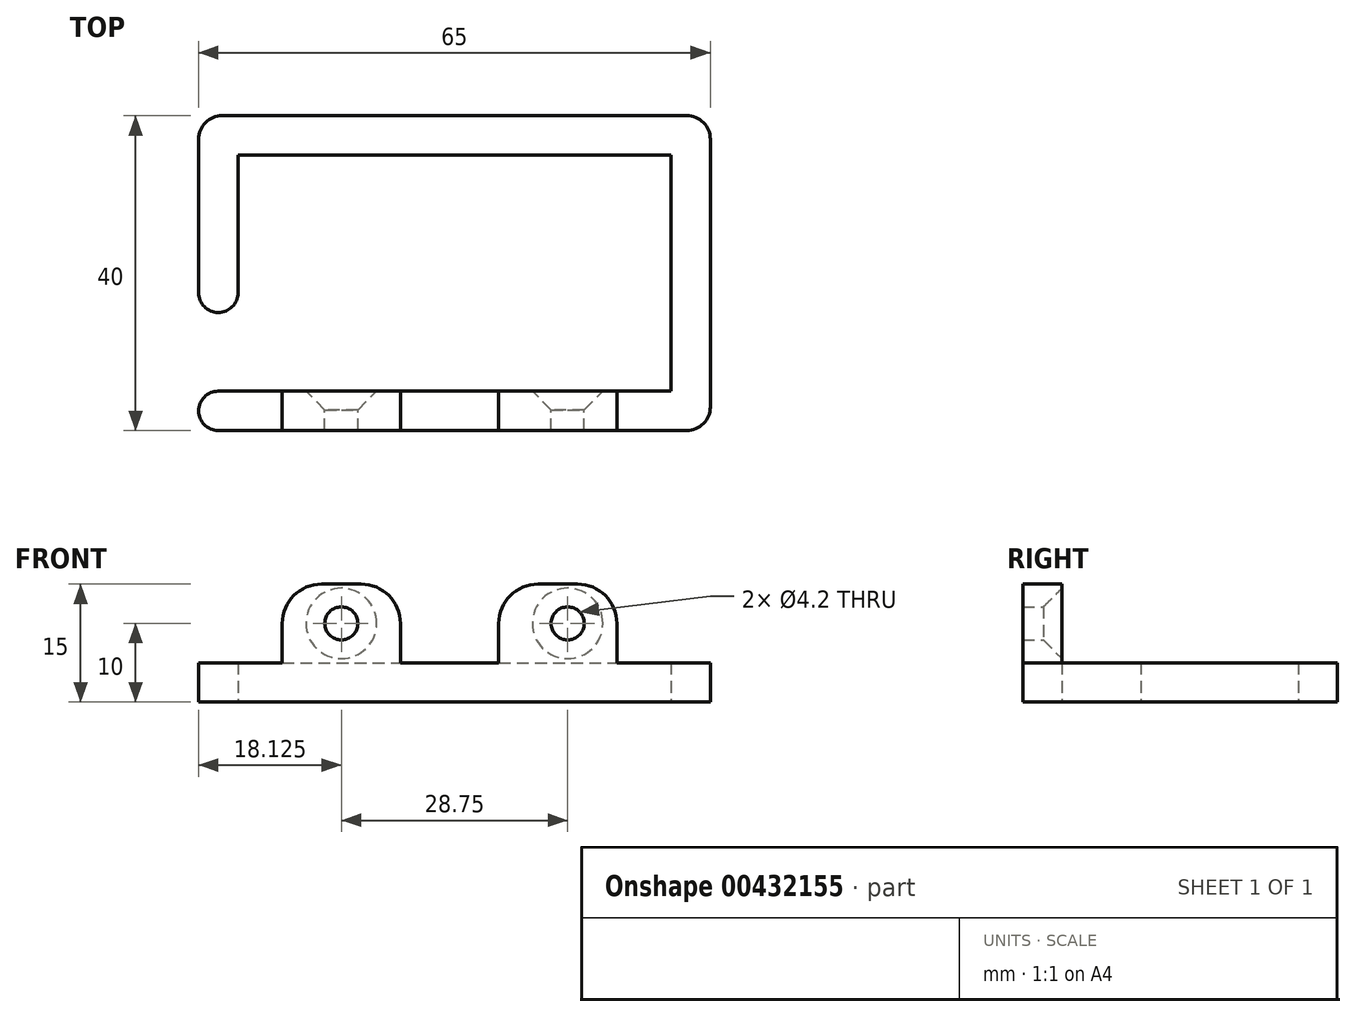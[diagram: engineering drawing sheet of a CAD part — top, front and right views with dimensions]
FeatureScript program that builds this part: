
annotation { "Feature Type Name" : "Feature", "Feature Type Description" : "" }
export const myFeature = defineFeature(function(context is Context, id is Id, definition is map)
    precondition{}
    {
        {
            var Q0;
            Q0=qCreatedBy(makeId("Top.planeOp"),FACE);
            var sketch = newSketch(context, id + "F0", { "sketchPlane" : qUnion([Q0])});
            skLineSegment(sketch, "E0.bottom", {"start": v(-29.5, 20) * mm, "end": v(29.5, 20) * mm});
            skLineSegment(sketch, "E0.top", {"start": v(-30, -20) * mm, "end": v(29.5, -20) * mm});
            skLineSegment(sketch, "E0.left", {"start": v(-32.5, 17) * mm, "end": v(-32.5, -2.5) * mm});
            skLineSegment(sketch, "E0.right", {"start": v(32.5, 17) * mm, "end": v(32.5, -17) * mm});
            skPoint(sketch, "E1.visualSharp", {"position": v(-32.5, 20) * mm});
            skArc(sketch, "E1.filletArc", {"start": v(-29.5, 20) * mm, "mid": v(-31.62, 19.12) * mm, "end": v(-32.5, 17) * mm});
            skPoint(sketch, "E2.visualSharp", {"position": v(-32.5, -20) * mm});
            skPoint(sketch, "E3.visualSharp", {"position": v(32.5, -20) * mm});
            skArc(sketch, "E3.filletArc", {"start": v(29.5, -20) * mm, "mid": v(31.62, -19.12) * mm, "end": v(32.5, -17) * mm});
            skPoint(sketch, "E4.visualSharp", {"position": v(32.5, 20) * mm});
            skArc(sketch, "E4.filletArc", {"start": v(32.5, 17) * mm, "mid": v(31.62, 19.12) * mm, "end": v(29.5, 20) * mm});
            skLineSegment(sketch, "E5.0", {"start": v(-27.5, 15) * mm, "end": v(27.5, 15) * mm});
            skLineSegment(sketch, "E5.1", {"start": v(-27.5, 15) * mm, "end": v(-27.5, -2.5) * mm});
            skLineSegment(sketch, "E5.2", {"start": v(-27.5, -15) * mm, "end": v(27.5, -15) * mm});
            skLineSegment(sketch, "E5.3", {"start": v(27.5, 15) * mm, "end": v(27.5, -15) * mm});
            skLineSegment(sketch, "E6", {"start": v(-27.5, -15) * mm, "end": v(-30, -15) * mm});
            skLineSegment(sketch, "E7", {"start": v(-32.5, -17.5) * mm, "end": v(-32.5, -17.5) * mm});
            skLineSegment(sketch, "E8", {"start": v(-30, -5) * mm, "end": v(-30, -5) * mm});
            skPoint(sketch, "E9.visualSharp", {"position": v(-32.5, -15) * mm});
            skArc(sketch, "E9.filletArc", {"start": v(-30, -15) * mm, "mid": v(-31.77, -15.73) * mm, "end": v(-32.5, -17.5) * mm});
            skArc(sketch, "E10.filletArc", {"start": v(-32.5, -17.5) * mm, "mid": v(-31.77, -19.27) * mm, "end": v(-30, -20) * mm});
            skPoint(sketch, "E11.visualSharp", {"position": v(-32.5, -5) * mm});
            skArc(sketch, "E11.filletArc", {"start": v(-32.5, -2.5) * mm, "mid": v(-31.77, -4.27) * mm, "end": v(-30, -5) * mm});
            skPoint(sketch, "E12.visualSharp", {"position": v(-27.5, -5) * mm});
            skArc(sketch, "E12.filletArc", {"start": v(-30, -5) * mm, "mid": v(-28.23, -4.27) * mm, "end": v(-27.5, -2.5) * mm});
            skSolve(sketch);
        }
        {
            var Q0;
            Q0=makeQuery(id+"F0.imprint","IMPRINT",FACE,{"disambiguationData":[TD([[makeQuery(id+"F0.imprint","IMPRINT",EDGE,{"derivedFrom":sQuery(id+"F0.wireOp",EDGE,"E0.bottom")}),-1.0]])]});
            extrude(context, id + "F1", {"entities" : qUnion([Q0]), "depth" : 5 * mm});
        }
        {
            var Q0;
            Q0=makeQuery(id+"F1.opExtrude","CAP_FACE",FACE,{"disambiguationData":[OSD([sQuery(id+"F0.wireOp",EDGE,"E0.bottom"),sQuery(id+"F0.wireOp",EDGE,"E0.top"),sQuery(id+"F0.wireOp",EDGE,"E0.left"),sQuery(id+"F0.wireOp",EDGE,"E0.right"),sQuery(id+"F0.wireOp",EDGE,"E1.filletArc"),sQuery(id+"F0.wireOp",EDGE,"E2.filletArc"),sQuery(id+"F0.wireOp",EDGE,"E3.filletArc"),sQuery(id+"F0.wireOp",EDGE,"E4.filletArc"),sQuery(id+"F0.wireOp",EDGE,"E5.0"),sQuery(id+"F0.wireOp",EDGE,"E5.1"),sQuery(id+"F0.wireOp",EDGE,"E5.2"),sQuery(id+"F0.wireOp",EDGE,"E5.3")])],"isStart":false});
            var sketch = newSketch(context, id + "F2", { "sketchPlane" : qUnion([Q0])});
            skLineSegment(sketch, "E13", {"start": v(27.5, -15) * mm, "end": v(-1.25, -15) * mm, "construction": true});
            skLineSegment(sketch, "E14", {"start": v(-1.25, -15) * mm, "end": v(-27.5, 15) * mm, "construction": true});
            skLineSegment(sketch, "E15", {"start": v(-14.37, 0) * mm, "end": v(-14.37, -20) * mm, "construction": true});
            skLineSegment(sketch, "E16", {"start": v(13.13, -15) * mm, "end": v(13.13, -20) * mm, "construction": true});
            skLineSegment(sketch, "E17.bottom", {"start": v(-21.87, -15) * mm, "end": v(-6.87, -15) * mm});
            skLineSegment(sketch, "E17.top", {"start": v(-21.87, -20) * mm, "end": v(-6.87, -20) * mm});
            skLineSegment(sketch, "E17.left", {"start": v(-21.87, -15) * mm, "end": v(-21.87, -20) * mm});
            skLineSegment(sketch, "E17.right", {"start": v(-6.87, -15) * mm, "end": v(-6.87, -20) * mm});
            skLineSegment(sketch, "E18.bottom", {"start": v(5.63, -15) * mm, "end": v(20.62, -15) * mm});
            skLineSegment(sketch, "E18.top", {"start": v(5.63, -20) * mm, "end": v(20.62, -20) * mm});
            skLineSegment(sketch, "E18.left", {"start": v(5.63, -15) * mm, "end": v(5.63, -20) * mm});
            skLineSegment(sketch, "E18.right", {"start": v(20.62, -15) * mm, "end": v(20.62, -20) * mm});
            skSolve(sketch);
        }
        {
            var Q0;
            Q0=makeQuery(id+"F2.imprint","IMPRINT",FACE,{"disambiguationData":[TD([[makeQuery(id+"F2.imprint","IMPRINT",EDGE,{"derivedFrom":sQuery(id+"F2.wireOp",EDGE,"E17.bottom")}),-1.0]])]});
            var Q1;
            Q1=makeQuery(id+"F2.imprint","IMPRINT",FACE,{"disambiguationData":[TD([[makeQuery(id+"F2.imprint","IMPRINT",EDGE,{"derivedFrom":sQuery(id+"F2.wireOp",EDGE,"E18.bottom")}),-1.0]])]});
            extrude(context, id + "F3", {"entities" : qUnion([Q0, Q1]), "operationType" : NewBodyOperationType.ADD, "depth" : 10 * mm});
        }
        {
            var Q0;
            Q0=makeQuery(id+"F3.opExtrude","CAP_EDGE",EDGE,{"disambiguationData":[OSD([sQuery(id+"F2.wireOp",EDGE,"E17.left")])],"isStart":false});
            var Q1;
            Q1=makeQuery(id+"F3.opExtrude","CAP_EDGE",EDGE,{"disambiguationData":[OSD([sQuery(id+"F2.wireOp",EDGE,"E17.right")])],"isStart":false});
            var Q2;
            Q2=makeQuery(id+"F3.opExtrude","CAP_EDGE",EDGE,{"disambiguationData":[OSD([sQuery(id+"F2.wireOp",EDGE,"E18.left")])],"isStart":false});
            var Q3;
            Q3=makeQuery(id+"F3.opExtrude","CAP_EDGE",EDGE,{"disambiguationData":[OSD([sQuery(id+"F2.wireOp",EDGE,"E18.right")])],"isStart":false});
            fillet(context, id + "F4", {"entities" : qUnion([Q0, Q1, Q2, Q3]), "radius" : 5 * mm, "tangentPropagation" : true, "allowEdgeOverflow" : false});
        }
        {
            var Q0;
            Q0=makeQuery(id+"F3.boolean.opBoolean","MERGE",FACE,{"derivedFrom":[makeQuery(id+"F1.opExtrude","SWEPT_FACE",FACE,{"disambiguationData":[OSD([sQuery(id+"F0.wireOp",EDGE,"E5.2")])]}),makeQuery(id+"F3.opExtrude","SWEPT_FACE",FACE,{"disambiguationData":[OSD([sQuery(id+"F2.wireOp",EDGE,"E17.bottom")])]}),makeQuery(id+"F3.opExtrude","SWEPT_FACE",FACE,{"disambiguationData":[OSD([sQuery(id+"F2.wireOp",EDGE,"E18.bottom")])]})]});
            var sketch = newSketch(context, id + "F5", { "sketchPlane" : qUnion([Q0])});
            skLineSegment(sketch, "E19", {"start": v(21.87, 5) * mm, "end": v(6.87, 5) * mm, "construction": true});
            skLineSegment(sketch, "E20", {"start": v(14.37, 5) * mm, "end": v(14.37, 15) * mm, "construction": true});
            skPoint(sketch, "E21", {"position": v(14.37, 10) * mm});
            skPoint(sketch, "E22.MirrorP", {"position": v(-14.37, 10) * mm});
            skSolve(sketch);
        }
        {
            var Q0;
            Q0=sQuery(id+"F5.wireOp",VERTEX,"E21");
            var Q1;
            Q1=sQuery(id+"F5.wireOp",VERTEX,"E22.MirrorP");
            var Q2;
            Q2=makeQuery(id+"F1.opExtrude","SWEPT_BODY",BODY,{"disambiguationData":[OSD([sQuery(id+"F0.wireOp",EDGE,"E0.bottom"),sQuery(id+"F0.wireOp",EDGE,"E0.top"),sQuery(id+"F0.wireOp",EDGE,"E0.left"),sQuery(id+"F0.wireOp",EDGE,"E0.right"),sQuery(id+"F0.wireOp",EDGE,"E1.filletArc"),sQuery(id+"F0.wireOp",EDGE,"E2.filletArc"),sQuery(id+"F0.wireOp",EDGE,"E3.filletArc"),sQuery(id+"F0.wireOp",EDGE,"E4.filletArc"),sQuery(id+"F0.wireOp",EDGE,"E5.0"),sQuery(id+"F0.wireOp",EDGE,"E5.1"),sQuery(id+"F0.wireOp",EDGE,"E5.2"),sQuery(id+"F0.wireOp",EDGE,"E5.3")])]});
            hole(context, id + "F6", {"style" : HoleStyle.C_SINK, "endStyle" : HoleEndStyle.THROUGH, "holeDiameter" : 4.2 * mm, "cSinkDiameter" : 8.96 * mm, "cSinkAngle" : 90 * degree, "isTappedThrough" : true, "tappedDepth" : 12 * mm, "tapClearance" : 3, "locations" : qUnion([Q0, Q1]), "scope" : qUnion([Q2])});
        }
    });
